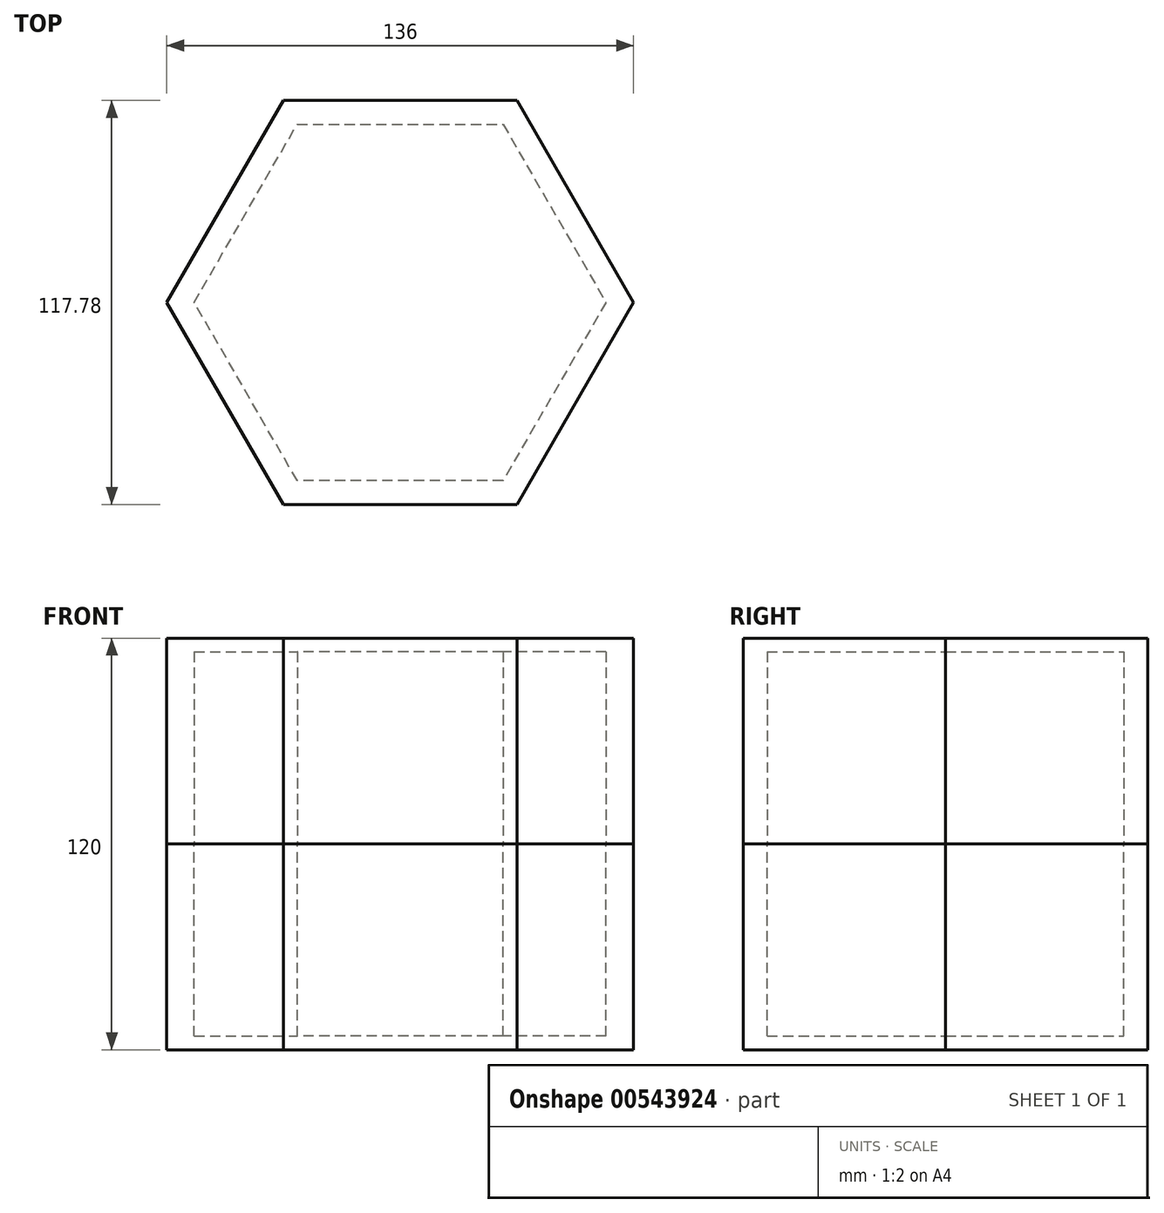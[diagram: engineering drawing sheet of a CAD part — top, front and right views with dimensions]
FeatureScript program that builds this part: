
annotation { "Feature Type Name" : "Feature", "Feature Type Description" : "" }
export const myFeature = defineFeature(function(context is Context, id is Id, definition is map)
    precondition{}
    {
        {
            var Q0;
            Q0=qCreatedBy(makeId("Top.planeOp"),FACE);
            var sketch = newSketch(context, id + "F0", { "sketchPlane" : qUnion([Q0])});
            skLineSegment(sketch, "E0", {"start": v(-60, 0) * mm, "end": v(-30, 51.96) * mm});
            skLineSegment(sketch, "E1", {"start": v(-30, 51.96) * mm, "end": v(30, 51.96) * mm});
            skLineSegment(sketch, "E2", {"start": v(30, 51.96) * mm, "end": v(60, 0) * mm});
            skLineSegment(sketch, "E3", {"start": v(60, 0) * mm, "end": v(30, -51.96) * mm});
            skLineSegment(sketch, "E4", {"start": v(30, -51.96) * mm, "end": v(-30, -51.96) * mm});
            skLineSegment(sketch, "E5", {"start": v(-30, -51.96) * mm, "end": v(-60, 0) * mm});
            skLineSegment(sketch, "E6", {"start": v(0, 51.96) * mm, "end": v(0, 0) * mm, "construction": true});
            skLineSegment(sketch, "E7", {"start": v(0, 0) * mm, "end": v(0, -51.96) * mm, "construction": true});
            skLineSegment(sketch, "E8", {"start": v(-60, 0) * mm, "end": v(0, 0) * mm, "construction": true});
            skLineSegment(sketch, "E9", {"start": v(60, 0) * mm, "end": v(0, 0) * mm, "construction": true});
            skSolve(sketch);
        }
        {
            var Q0;
            Q0=qCreatedBy(makeId("Top.planeOp"),FACE);
            var sketch = newSketch(context, id + "F1", { "sketchPlane" : qUnion([Q0])});
            skLineSegment(sketch, "E10", {"start": v(-68, 0) * mm, "end": v(-34, 58.89) * mm});
            skLineSegment(sketch, "E11", {"start": v(-34, 58.89) * mm, "end": v(34, 58.89) * mm});
            skLineSegment(sketch, "E12", {"start": v(34, 58.89) * mm, "end": v(68, 0) * mm});
            skLineSegment(sketch, "E13", {"start": v(68, 0) * mm, "end": v(34, -58.89) * mm});
            skLineSegment(sketch, "E14", {"start": v(34, -58.89) * mm, "end": v(-34, -58.89) * mm});
            skLineSegment(sketch, "E15", {"start": v(-34, -58.89) * mm, "end": v(-68, 0) * mm});
            skLineSegment(sketch, "E16", {"start": v(0, 58.89) * mm, "end": v(0, 0) * mm, "construction": true});
            skLineSegment(sketch, "E17", {"start": v(0, 0) * mm, "end": v(0, -58.89) * mm, "construction": true});
            skLineSegment(sketch, "E18", {"start": v(-68, 0) * mm, "end": v(0, 0) * mm, "construction": true});
            skLineSegment(sketch, "E19", {"start": v(68, 0) * mm, "end": v(0, 0) * mm, "construction": true});
            skSolve(sketch);
        }
        {
            var Q0;
            Q0 = qSketchRegion(id + "F1", true);
            extrude(context, id + "F2", {"entities" : qUnion([Q0]), "depth" : 60 * mm, "offsetDistance" : 25 * mm});
        }
        {
            var Q0;
            Q0 = qSketchRegion(id + "F0", true);
            extrude(context, id + "F3", {"entities" : qUnion([Q0]), "operationType" : NewBodyOperationType.REMOVE, "depth" : 56 * mm, "offsetDistance" : 25 * mm});
        }
        {
            var Q0;
            Q0=makeQuery(id+"F2.opExtrude","SWEPT_BODY",BODY,{"disambiguationData":[OSD([sQuery(id+"F1.wireOp",EDGE,"E10"),sQuery(id+"F1.wireOp",EDGE,"E11"),sQuery(id+"F1.wireOp",EDGE,"E12"),sQuery(id+"F1.wireOp",EDGE,"E13"),sQuery(id+"F1.wireOp",EDGE,"E14"),sQuery(id+"F1.wireOp",EDGE,"E15")])]});
            var Q1;
            Q1=qCreatedBy(makeId("Top.planeOp"),FACE);
            mirror(context, id + "F4", {"entities" : qUnion([Q0]), "mirrorPlane" : qUnion([Q1])});
        }
    });
